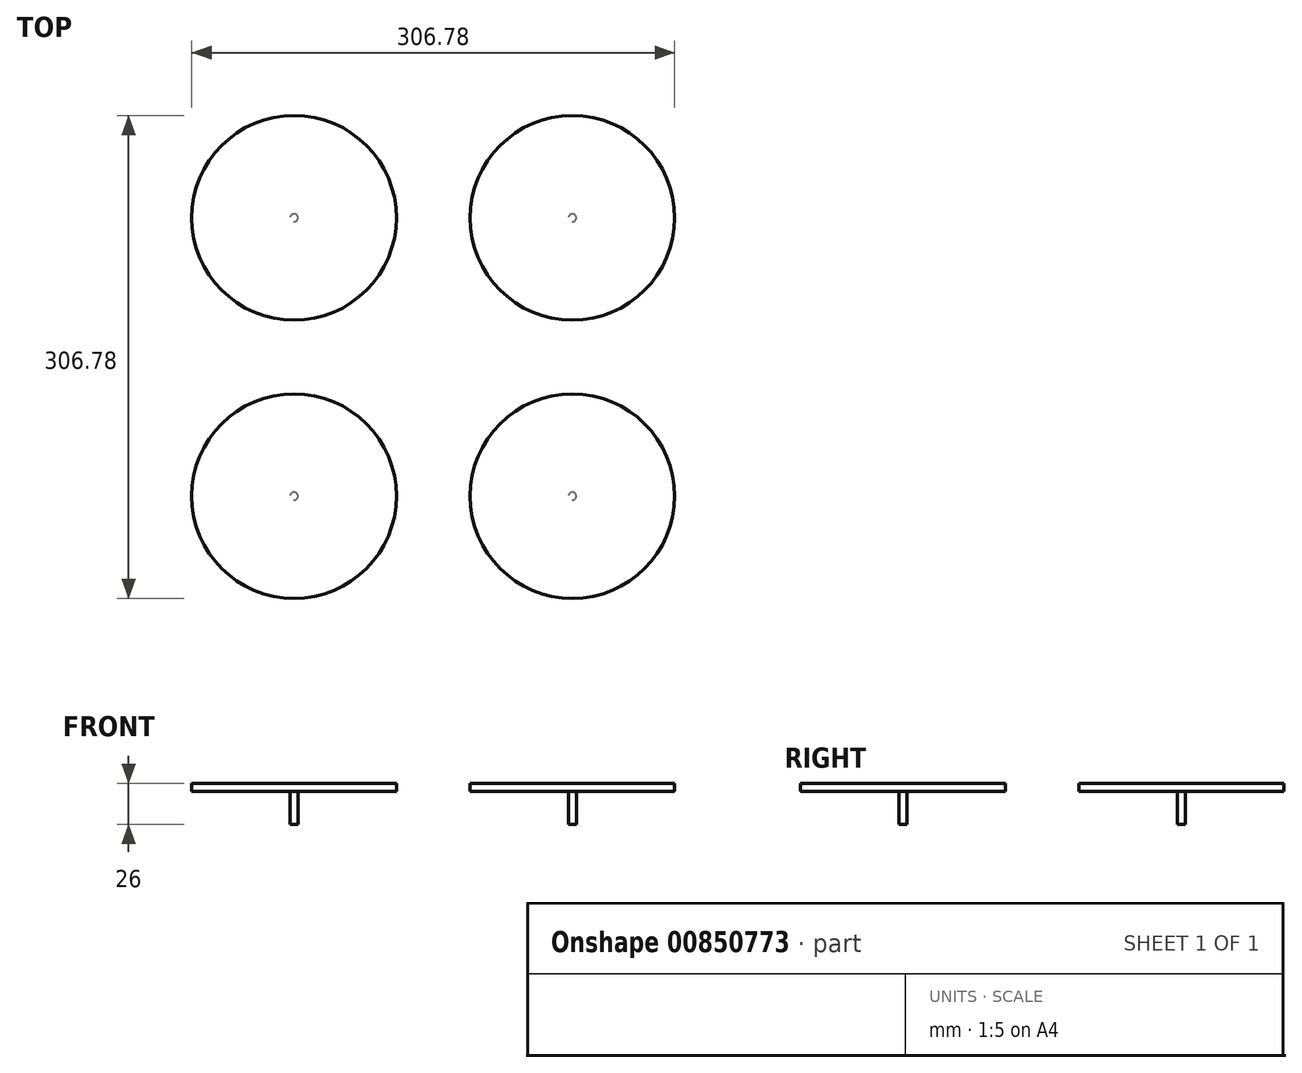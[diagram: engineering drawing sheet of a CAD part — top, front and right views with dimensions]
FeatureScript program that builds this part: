
annotation { "Feature Type Name" : "Feature", "Feature Type Description" : "" }
export const myFeature = defineFeature(function(context is Context, id is Id, definition is map)
    precondition{}
    {
        {
            var Q0;
            Q0=qCreatedBy(makeId("Top.planeOp"),FACE);
            var sketch = newSketch(context, id + "F0", { "sketchPlane" : qUnion([Q0])});
            skLineSegment(sketch, "E0", {"start": v(0, 0) * mm, "end": v(88.39, 88.39) * mm, "construction": true});
            skCircle(sketch, "E1", {"center": v(88.39, 88.39) * mm, "radius": 2.5 * mm});
            skSolve(sketch);
        }
        {
            var Q0;
            Q0 = qSketchRegion(id + "F0", true);
            extrude(context, id + "F1", {"entities" : qUnion([Q0]), "depth" : 21 * mm, "offsetDistance" : 25 * mm});
        }
        {
            var Q0;
            Q0=makeQuery(id+"F1.opExtrude","CAP_FACE",FACE,{"disambiguationData":[OSD([sQuery(id+"F0.wireOp",EDGE,"E1")])],"isStart":false});
            var sketch = newSketch(context, id + "F2", { "sketchPlane" : qUnion([Q0])});
            skCircle(sketch, "E2", {"center": v(88.39, 88.39) * mm, "radius": 65 * mm});
            skSolve(sketch);
        }
        {
            var Q0;
            Q0 = qSketchRegion(id + "F2", true);
            extrude(context, id + "F3", {"entities" : qUnion([Q0]), "operationType" : NewBodyOperationType.ADD, "depth" : 5 * mm, "offsetDistance" : 25 * mm});
        }
        {
            var Q0;
            Q0=makeQuery(id+"F1.opExtrude","SWEPT_BODY",BODY,{"disambiguationData":[OSD([sQuery(id+"F0.wireOp",EDGE,"E1")])]});
            var Q1;
            Q1=qCreatedBy(makeId("Right.planeOp"),FACE);
            mirror(context, id + "F4", {"entities" : qUnion([Q0]), "mirrorPlane" : qUnion([Q1])});
        }
        {
            var Q0;
            Q0=makeQuery(id+"F4.opPattern","COPY",BODY,{"derivedFrom":makeQuery(id+"F1.opExtrude","SWEPT_BODY",BODY,{"disambiguationData":[OSD([sQuery(id+"F0.wireOp",EDGE,"E1")])]}),"instanceName":"1"});
            var Q1;
            Q1=makeQuery(id+"F1.opExtrude","SWEPT_BODY",BODY,{"disambiguationData":[OSD([sQuery(id+"F0.wireOp",EDGE,"E1")])]});
            var Q2;
            Q2=qCreatedBy(makeId("Front.planeOp"),FACE);
            mirror(context, id + "F5", {"entities" : qUnion([Q0, Q1]), "mirrorPlane" : qUnion([Q2])});
        }
    });
